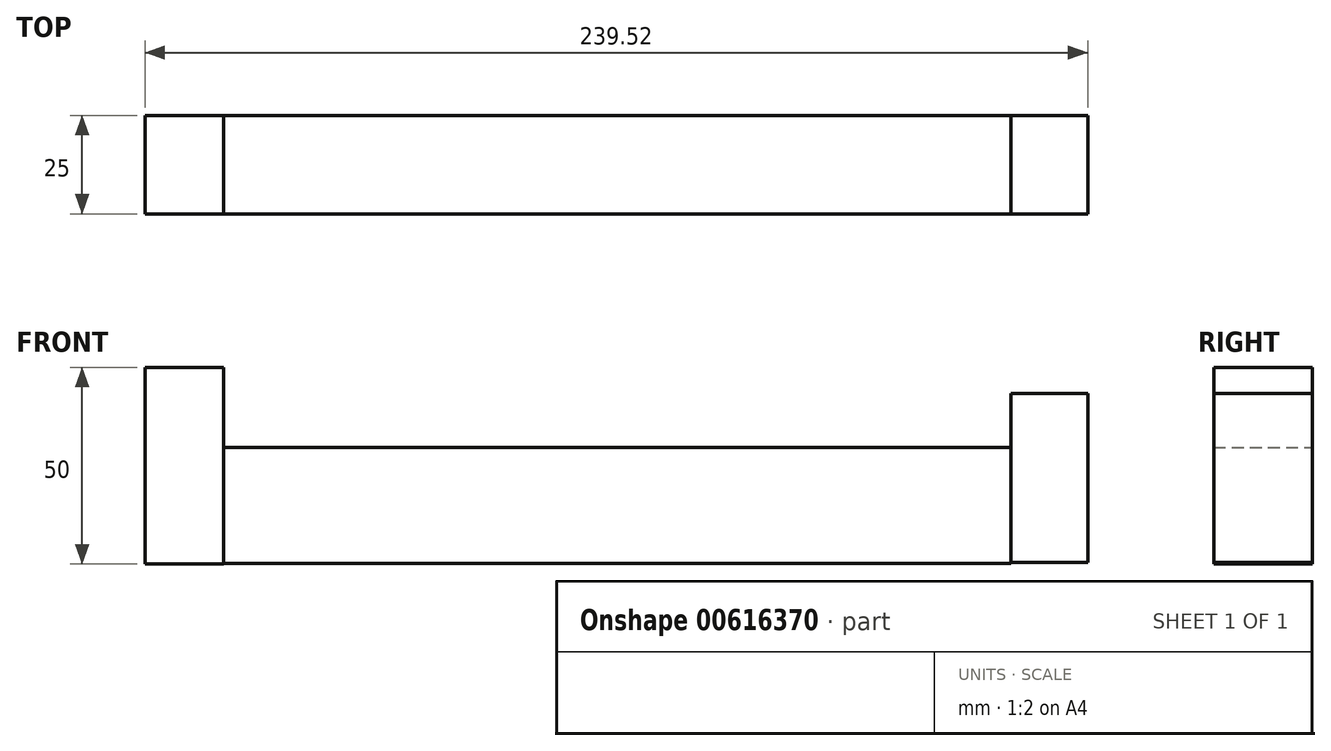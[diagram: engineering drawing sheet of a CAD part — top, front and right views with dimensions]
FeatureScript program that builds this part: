
annotation { "Feature Type Name" : "Feature", "Feature Type Description" : "" }
export const myFeature = defineFeature(function(context is Context, id is Id, definition is map)
    precondition{}
    {
        {
            var Q0;
            Q0=qCreatedBy(makeId("Front.planeOp"),FACE);
            var sketch = newSketch(context, id + "F0", { "sketchPlane" : qUnion([Q0])});
            skLineSegment(sketch, "E0.bottom", {"start": v(-151.28, 37.62) * mm, "end": v(-131.28, 37.62) * mm});
            skLineSegment(sketch, "E0.top", {"start": v(-151.28, -12.38) * mm, "end": v(-131.28, -12.38) * mm});
            skLineSegment(sketch, "E0.left", {"start": v(-151.28, 37.62) * mm, "end": v(-151.28, -12.38) * mm});
            skLineSegment(sketch, "E0.right", {"start": v(-131.28, 37.62) * mm, "end": v(-131.28, -12.38) * mm});
            skSolve(sketch);
        }
        {
            var Q0;
            Q0=qCreatedBy(makeId("Front.planeOp"),FACE);
            var sketch = newSketch(context, id + "F1", { "sketchPlane" : qUnion([Q0])});
            skLineSegment(sketch, "E1.bottom", {"start": v(-131.26, -12.22) * mm, "end": v(68.74, -12.22) * mm});
            skLineSegment(sketch, "E1.top", {"start": v(-131.26, 17.26) * mm, "end": v(68.74, 17.26) * mm});
            skLineSegment(sketch, "E1.left", {"start": v(-131.26, -12.22) * mm, "end": v(-131.26, 17.26) * mm});
            skLineSegment(sketch, "E1.right", {"start": v(68.74, -12.22) * mm, "end": v(68.74, 17.26) * mm});
            skSolve(sketch);
        }
        {
            var Q0;
            Q0=qCreatedBy(makeId("Front.planeOp"),FACE);
            var sketch = newSketch(context, id + "F2", { "sketchPlane" : qUnion([Q0])});
            skLineSegment(sketch, "E2.bottom", {"start": v(68.7, -11.99) * mm, "end": v(88.24, -11.99) * mm});
            skLineSegment(sketch, "E2.top", {"start": v(68.7, 30.93) * mm, "end": v(88.24, 30.93) * mm});
            skLineSegment(sketch, "E2.left", {"start": v(68.7, -11.99) * mm, "end": v(68.7, 30.93) * mm});
            skLineSegment(sketch, "E2.right", {"start": v(88.24, -11.99) * mm, "end": v(88.24, 30.93) * mm});
            skSolve(sketch);
        }
        {
            var Q0;
            Q0=makeQuery(id+"F0.imprint","IMPRINT",FACE,{"disambiguationData":[TD([[makeQuery(id+"F0.imprint","IMPRINT",EDGE,{"derivedFrom":sQuery(id+"F0.wireOp",EDGE,"E0.bottom")}),-1.0]])]});
            var Q1;
            Q1=makeQuery(id+"F1.imprint","IMPRINT",FACE,{"disambiguationData":[TD([[makeQuery(id+"F1.imprint","IMPRINT",EDGE,{"derivedFrom":sQuery(id+"F1.wireOp",EDGE,"E1.bottom")}),1.0]])]});
            var Q2;
            Q2=makeQuery(id+"F2.imprint","IMPRINT",FACE,{"disambiguationData":[TD([[makeQuery(id+"F2.imprint","IMPRINT",EDGE,{"derivedFrom":sQuery(id+"F2.wireOp",EDGE,"E2.bottom")}),1.0]])]});
            extrude(context, id + "F3", {"entities" : qUnion([Q0, Q1, Q2]), "depth" : 25 * mm, "offsetDistance" : 25 * mm});
        }
    });
